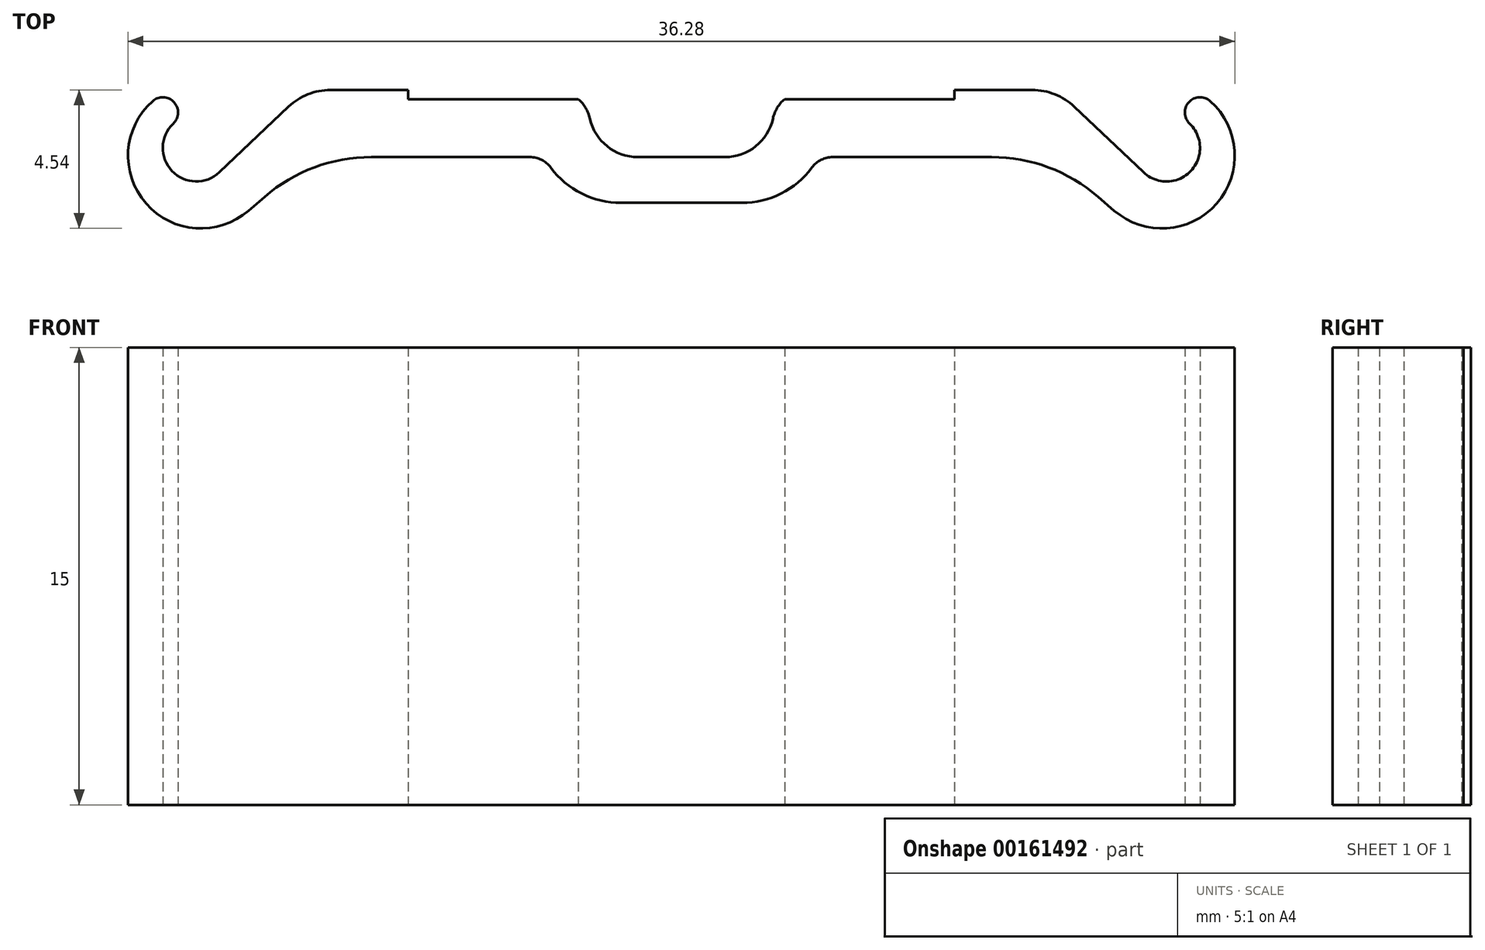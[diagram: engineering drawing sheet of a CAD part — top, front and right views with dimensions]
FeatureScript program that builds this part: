
annotation { "Feature Type Name" : "Feature", "Feature Type Description" : "" }
export const myFeature = defineFeature(function(context is Context, id is Id, definition is map)
    precondition{}
    {
        {
            var Q0;
            Q0=qCreatedBy(makeId("Top.planeOp"),FACE);
            var sketch = newSketch(context, id + "F0", { "sketchPlane" : qUnion([Q0])});
            skLineSegment(sketch, "E0", {"start": v(0, 0) * mm, "end": v(12.38, 0) * mm, "construction": true});
            skLineSegment(sketch, "E1", {"start": v(13.75, -0.55) * mm, "end": v(16.66, -3.3) * mm, "construction": true});
            skArc(sketch, "E2", {"start": v(16.66, -3.3) * mm, "mid": v(16.7, -4.86) * mm, "end": v(15.14, -4.9) * mm, "construction": true});
            skLineSegment(sketch, "E3", {"start": v(15.14, -4.9) * mm, "end": v(12.88, -2.75) * mm, "construction": true});
            skLineSegment(sketch, "E4", {"start": v(11.5, -2.2) * mm, "end": v(8.95, -2.2) * mm, "construction": true});
            skPoint(sketch, "E5.visualSharp", {"position": v(12.3, -2.2) * mm});
            skArc(sketch, "E5.filletArc", {"start": v(12.88, -2.75) * mm, "mid": v(12.24, -2.34) * mm, "end": v(11.5, -2.2) * mm, "construction": true});
            skPoint(sketch, "E6.visualSharp", {"position": v(13.17, 0) * mm});
            skArc(sketch, "E6.filletArc", {"start": v(13.75, -0.55) * mm, "mid": v(13.12, -0.14) * mm, "end": v(12.38, 0) * mm, "construction": true});
            skLineSegment(sketch, "E7", {"start": v(8.95, -2.2) * mm, "end": v(11.5, -2.2) * mm});
            skArc(sketch, "E8", {"start": v(11.5, -2.2) * mm, "mid": v(12.24, -2.34) * mm, "end": v(12.88, -2.75) * mm});
            skLineSegment(sketch, "E9", {"start": v(12.88, -2.75) * mm, "end": v(15.14, -4.9) * mm});
            skArc(sketch, "E10", {"start": v(15.14, -4.9) * mm, "mid": v(16.7, -4.86) * mm, "end": v(16.66, -3.3) * mm});
            skArc(sketch, "E11", {"start": v(16.66, -3.3) * mm, "mid": v(16.63, -2.6) * mm, "end": v(17.33, -2.56) * mm});
            skArc(sketch, "E12", {"start": v(17.33, -2.56) * mm, "mid": v(17.55, -5.92) * mm, "end": v(14.19, -6.16) * mm});
            skLineSegment(sketch, "E13", {"start": v(14.19, -6.16) * mm, "end": v(13.66, -5.7) * mm});
            skArc(sketch, "E14", {"start": v(13.66, -5.7) * mm, "mid": v(12.03, -4.74) * mm, "end": v(10.16, -4.4) * mm});
            skLineSegment(sketch, "E15", {"start": v(10.16, -4.4) * mm, "end": v(4.96, -4.4) * mm});
            skLineSegment(sketch, "E16", {"start": v(0, -5.9) * mm, "end": v(1.98, -5.9) * mm});
            skArc(sketch, "E17", {"start": v(1.98, -5.9) * mm, "mid": v(3.27, -5.6) * mm, "end": v(4.28, -4.74) * mm});
            skArc(sketch, "E18", {"start": v(4.28, -4.74) * mm, "mid": v(4.58, -4.5) * mm, "end": v(4.96, -4.4) * mm});
            skPoint(sketch, "E19.orphan", {"position": v(0, -4.4) * mm});
            skLineSegment(sketch, "E20", {"start": v(0, -4.4) * mm, "end": v(1.43, -4.4) * mm});
            skArc(sketch, "E21", {"start": v(1.43, -4.4) * mm, "mid": v(2.43, -4.05) * mm, "end": v(3, -3.14) * mm});
            skArc(sketch, "E22", {"start": v(3, -3.14) * mm, "mid": v(3.14, -2.8) * mm, "end": v(3.38, -2.5) * mm});
            skArc(sketch, "E23.MirrorCS", {"start": v(-12.88, -2.75) * mm, "mid": v(-12.24, -2.34) * mm, "end": v(-11.5, -2.2) * mm, "construction": true});
            skArc(sketch, "E24.MirrorCS", {"start": v(-11.5, -2.2) * mm, "mid": v(-12.24, -2.34) * mm, "end": v(-12.88, -2.75) * mm});
            skLineSegment(sketch, "E25.MirrorCS", {"start": v(-14.19, -6.16) * mm, "end": v(-13.66, -5.7) * mm});
            skArc(sketch, "E26.MirrorCS", {"start": v(-16.66, -3.3) * mm, "mid": v(-16.7, -4.86) * mm, "end": v(-15.14, -4.9) * mm, "construction": true});
            skLineSegment(sketch, "E27.MirrorCS", {"start": v(-15.14, -4.9) * mm, "end": v(-12.88, -2.75) * mm, "construction": true});
            skArc(sketch, "E28.MirrorCS", {"start": v(-13.75, -0.55) * mm, "mid": v(-13.12, -0.14) * mm, "end": v(-12.38, 0) * mm, "construction": true});
            skLineSegment(sketch, "E29.MirrorCS", {"start": v(0, -5.9) * mm, "end": v(-1.98, -5.9) * mm});
            skLineSegment(sketch, "E30.MirrorCS", {"start": v(0, 0) * mm, "end": v(-12.38, 0) * mm, "construction": true});
            skArc(sketch, "E31.MirrorCS", {"start": v(-4.28, -4.74) * mm, "mid": v(-4.58, -4.5) * mm, "end": v(-4.96, -4.4) * mm});
            skLineSegment(sketch, "E32.MirrorCS", {"start": v(-11.5, -2.2) * mm, "end": v(-8.95, -2.2) * mm, "construction": true});
            skLineSegment(sketch, "E33.MirrorCS", {"start": v(-13.75, -0.55) * mm, "end": v(-16.66, -3.3) * mm, "construction": true});
            skArc(sketch, "E34.MirrorCS", {"start": v(-3, -3.14) * mm, "mid": v(-3.14, -2.8) * mm, "end": v(-3.38, -2.5) * mm});
            skPoint(sketch, "E35.MirrorP", {"position": v(-13.17, 0) * mm});
            skLineSegment(sketch, "E36.MirrorCS", {"start": v(-10.16, -4.4) * mm, "end": v(-4.96, -4.4) * mm});
            skLineSegment(sketch, "E37.MirrorCS", {"start": v(0, -4.4) * mm, "end": v(-1.43, -4.4) * mm});
            skPoint(sketch, "E38.MirrorP", {"position": v(-12.3, -2.2) * mm});
            skArc(sketch, "E39.MirrorCS", {"start": v(-13.66, -5.7) * mm, "mid": v(-12.03, -4.74) * mm, "end": v(-10.16, -4.4) * mm});
            skArc(sketch, "E40.MirrorCS", {"start": v(-1.43, -4.4) * mm, "mid": v(-2.43, -4.05) * mm, "end": v(-3, -3.14) * mm});
            skArc(sketch, "E41.MirrorCS", {"start": v(-17.33, -2.56) * mm, "mid": v(-17.55, -5.92) * mm, "end": v(-14.19, -6.16) * mm});
            skArc(sketch, "E42.MirrorCS", {"start": v(-16.66, -3.3) * mm, "mid": v(-16.63, -2.6) * mm, "end": v(-17.33, -2.56) * mm});
            skArc(sketch, "E43.MirrorCS", {"start": v(-15.14, -4.9) * mm, "mid": v(-16.7, -4.86) * mm, "end": v(-16.66, -3.3) * mm});
            skLineSegment(sketch, "E44.MirrorCS", {"start": v(-12.88, -2.75) * mm, "end": v(-15.14, -4.9) * mm});
            skLineSegment(sketch, "E45.MirrorCS", {"start": v(-8.95, -2.2) * mm, "end": v(-11.5, -2.2) * mm});
            skArc(sketch, "E46.MirrorCS", {"start": v(-1.98, -5.9) * mm, "mid": v(-3.27, -5.6) * mm, "end": v(-4.28, -4.74) * mm});
            skLineSegment(sketch, "E47", {"start": v(8.95, -2.2) * mm, "end": v(8.95, -2.5) * mm});
            skLineSegment(sketch, "E48", {"start": v(8.95, -2.5) * mm, "end": v(3.38, -2.5) * mm});
            skLineSegment(sketch, "E49.trimOffspring", {"start": v(4.18, -2.2) * mm, "end": v(0, -2.2) * mm, "construction": true});
            skPoint(sketch, "E50.orphan", {"position": v(0, -2.5) * mm});
            skLineSegment(sketch, "E51.MirrorCS", {"start": v(-8.95, -2.5) * mm, "end": v(-3.38, -2.5) * mm});
            skLineSegment(sketch, "E52.MirrorCS", {"start": v(-8.95, -2.2) * mm, "end": v(-8.95, -2.5) * mm});
            skLineSegment(sketch, "E53.trimOffspring", {"start": v(-4.18, -2.2) * mm, "end": v(0, -2.2) * mm, "construction": true});
            skSolve(sketch);
        }
        {
            var Q0;
            Q0=qSketchRegion(id+"F0",true);
            extrude(context, id + "F1", {"entities" : qUnion([Q0]), "depth" : 15 * mm});
        }
    });
